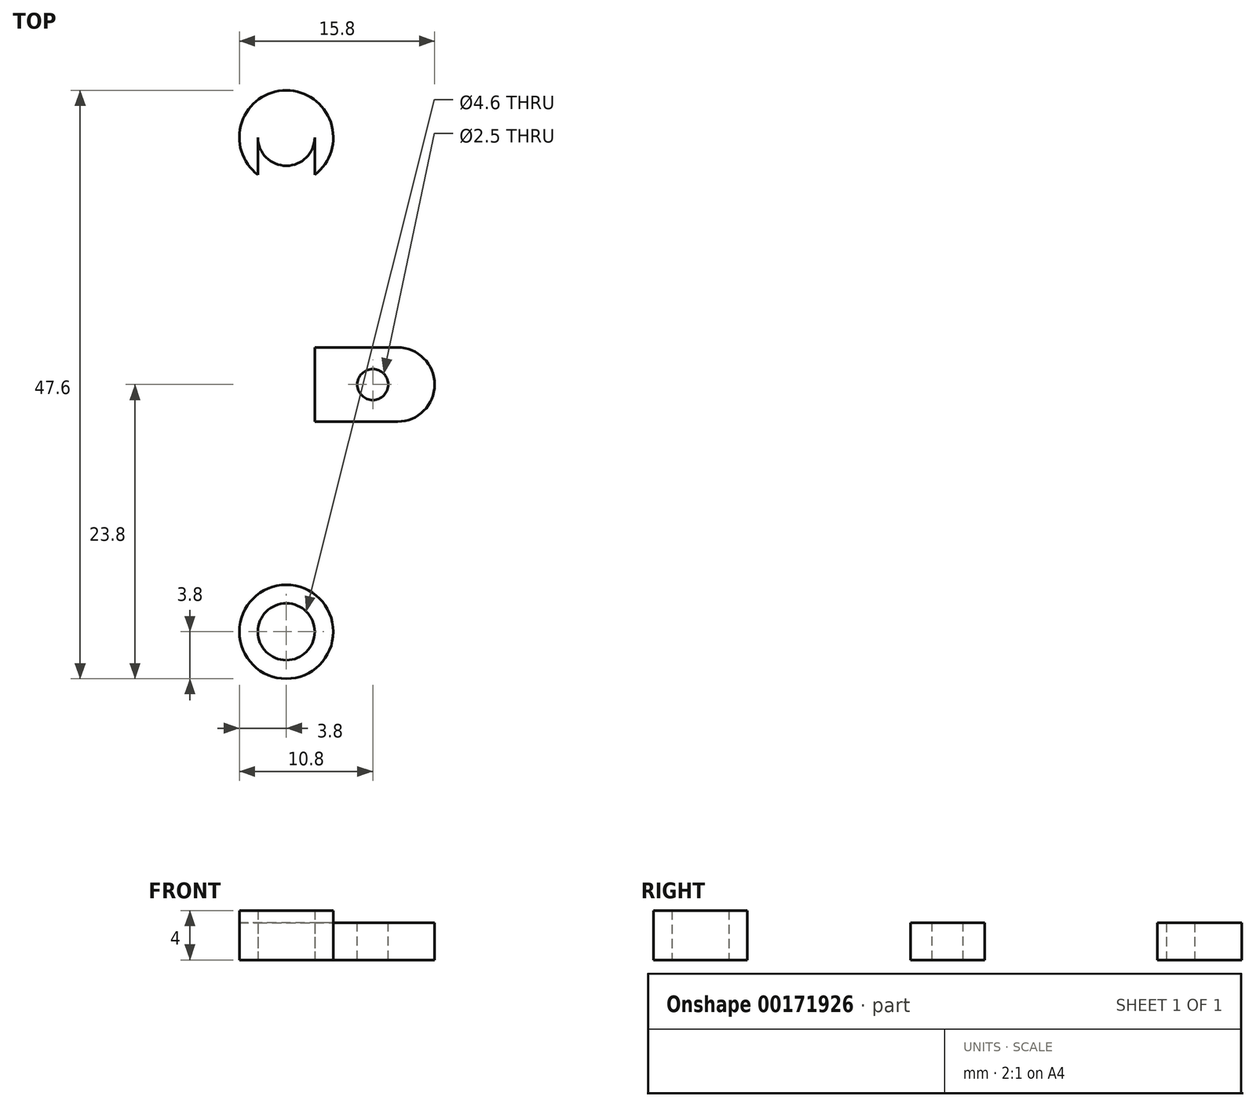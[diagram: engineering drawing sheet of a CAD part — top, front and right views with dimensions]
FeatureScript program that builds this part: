
annotation { "Feature Type Name" : "Feature", "Feature Type Description" : "" }
export const myFeature = defineFeature(function(context is Context, id is Id, definition is map)
    precondition{}
    {
        {
            var Q0;
            Q0=qCreatedBy(makeId("Top.planeOp"),FACE);
            var sketch = newSketch(context, id + "F0", { "sketchPlane" : qUnion([Q0])});
            skLineSegment(sketch, "E0.bottom", {"start": v(0, 0) * mm, "end": v(-17, 0) * mm, "construction": true});
            skLineSegment(sketch, "E0.top", {"start": v(0, 50) * mm, "end": v(-17, 50) * mm, "construction": true});
            skLineSegment(sketch, "E0.left", {"start": v(0, 0) * mm, "end": v(0, 50) * mm, "construction": true});
            skPoint(sketch, "E0.middle", {"position": v(-8.5, 25) * mm});
            skCircle(sketch, "E1", {"center": v(-12, 5) * mm, "radius": 2.3 * mm});
            skLineSegment(sketch, "E2", {"start": v(-18.53, 25) * mm, "end": v(0.77, 25) * mm, "construction": true});
            skCircle(sketch, "E3.MirrorC", {"center": v(-12, 45) * mm, "radius": 2.3 * mm});
            skLineSegment(sketch, "E4", {"start": v(-12, 50) * mm, "end": v(-8, 50) * mm});
            skLineSegment(sketch, "E5.right", {"start": v(0, 28) * mm, "end": v(0, 22) * mm});
            skCircle(sketch, "E6.0", {"center": v(-12, 45) * mm, "radius": 3.8 * mm});
            skCircle(sketch, "E7.0", {"center": v(-12, 5) * mm, "radius": 3.8 * mm});
            skLineSegment(sketch, "E8", {"start": v(-20.5, 45) * mm, "end": v(2.58, 45) * mm, "construction": true});
            skLineSegment(sketch, "E9", {"start": v(-20.08, 5) * mm, "end": v(6.27, 5) * mm, "construction": true});
            skLineSegment(sketch, "E10", {"start": v(-14.3, 45) * mm, "end": v(-14.3, 5) * mm});
            skLineSegment(sketch, "E11", {"start": v(-9.7, 5) * mm, "end": v(-9.7, 45) * mm});
            skLineSegment(sketch, "E12", {"start": v(0, 22) * mm, "end": v(-9.7, 22) * mm});
            skLineSegment(sketch, "E13", {"start": v(0, 28) * mm, "end": v(-9.7, 28) * mm});
            skSolve(sketch);
        }
        {
            var Q0;
            Q0=makeQuery(id+"F0.imprint","IMPRINT",FACE,{"disambiguationData":[TD([[makeQuery(id+"F0.imprint","IMPRINT",EDGE,{"derivedFrom":sQuery(id+"F0.wireOp",EDGE,"E5.bottom")}),-1.0]])]});
            var Q1;
            Q1=makeQuery(id+"F0.imprint","IMPRINT",FACE,{"disambiguationData":[TD([[makeQuery(id+"F0.imprint","IMPRINT",EDGE,{"derivedFrom":sQuery(id+"F0.wireOp",EDGE,"E1")}),-1.0]])]});
            var Q2;
            Q2=makeQuery(id+"F0.imprint","IMPRINT",FACE,{"disambiguationData":[TD([[makeQuery(id+"F0.imprint","IMPRINT",EDGE,{"derivedFrom":sQuery(id+"F0.wireOp",EDGE,"E3.MirrorC")}),1.0]])]});
            var Q3;
            {var subQ7=sQuery(id+"F0.wireOp",EDGE,"E5.left");Q3=makeQuery(id+"F0.imprint","IMPRINT",FACE,{"disambiguationData":[TD([[makeQuery(id+"F0.imprint","IMPRINT",EDGE,{"derivedFrom":subQ7}),-1.0]])]});}
            var Q4;
            {var subQ3=sQuery(id+"F0.wireOp",EDGE,"E6.0");var subQ5=makeQuery(id+"F0.imprint","IMPRINT",VERTEX,{"derivedFrom":subQ3});Q4=makeQuery(id+"F0.imprint","IMPRINT",FACE,{"disambiguationData":[TD([[makeQuery(id+"F0.imprint","IMPRINT",EDGE,{"disambiguationData":[TD([[subQ5,1.0]])],"derivedFrom":subQ3}),-1.0]])]});}
            var Q5;
            {var subQ4=sQuery(id+"F0.wireOp",EDGE,"E10");var subQ5=sQuery(id+"F0.wireOp",EDGE,"E6.0");var subQ6=makeQuery(id+"F0.imprint","INTERSECT",VERTEX,{"derivedFrom":[subQ5,subQ4]});Q5=makeQuery(id+"F0.imprint","IMPRINT",FACE,{"disambiguationData":[TD([[makeQuery(id+"F0.imprint","IMPRINT",EDGE,{"disambiguationData":[TD([[subQ6,1.0]])],"derivedFrom":subQ5}),1.0]])]});}
            var Q6;
            Q6=makeQuery(id+"F0.imprint","IMPRINT",FACE,{"disambiguationData":[TD([[makeQuery(id+"F0.imprint","IMPRINT",EDGE,{"derivedFrom":sQuery(id+"F0.wireOp",EDGE,"E5.right")}),-1.0]])]});
            var Q7;
            {var subQ6=sQuery(id+"F0.wireOp",EDGE,"E10");var subQ8=sQuery(id+"F0.wireOp",EDGE,"E3.MirrorC");var subQ10=makeQuery(id+"F0.imprint","INTERSECT",VERTEX,{"derivedFrom":[subQ8,subQ6]});Q7=makeQuery(id+"F0.imprint","IMPRINT",FACE,{"disambiguationData":[TD([[makeQuery(id+"F0.imprint","IMPRINT",EDGE,{"disambiguationData":[TD([[subQ10,-1.0]])],"derivedFrom":subQ8}),1.0]])]});}
            extrude(context, id + "F1", {"entities" : qUnion([Q0, Q1, Q2, Q3, Q4, Q5, Q6, Q7]), "depth" : 3 * mm});
        }
        {
            var Q0;
            Q0=makeQuery(id+"F1.opExtrude","CAP_FACE",FACE,{"disambiguationData":[OSD([sQuery(id+"F0.wireOp",EDGE,"E0.bottom"),sQuery(id+"F0.wireOp",EDGE,"E0.top"),sQuery(id+"F0.wireOp",EDGE,"E0.left"),sQuery(id+"F0.wireOp",EDGE,"E0.right"),sQuery(id+"F0.wireOp",EDGE,"E1"),sQuery(id+"F0.wireOp",EDGE,"E3.MirrorC")])],"isStart":false});
            var sketch = newSketch(context, id + "F2", { "sketchPlane" : qUnion([Q0])});
            skCircle(sketch, "E14", {"center": v(-5, 25) * mm, "radius": 1.25 * mm});
            skPoint(sketch, "E14.centerSnap0", {"position": v(-8.5, 0) * mm});
            skPoint(sketch, "E14.centerSnap1", {"position": v(0, 25) * mm});
            skSolve(sketch);
        }
        {
            var Q0;
            Q0 = qSketchRegion(id + "F2", true);
            extrude(context, id + "F3", {"entities" : qUnion([Q0]), "operationType" : NewBodyOperationType.REMOVE, "oppositeDirection" : true, "depth" : 25 * mm});
        }
        {
            var Q0;
            Q0=makeQuery(id+"F1.opExtrude","SWEPT_EDGE",EDGE,{"disambiguationData":[OSD([sQuery(id+"F0.wireOp",EDGE,"E0.left"),sQuery(id+"F0.wireOp",EDGE,"E5.top"),sQuery(id+"F0.wireOp",EDGE,"E5.right")])]});
            var Q1;
            Q1=makeQuery(id+"F1.opExtrude","SWEPT_EDGE",EDGE,{"disambiguationData":[OSD([sQuery(id+"F0.wireOp",EDGE,"E0.left"),sQuery(id+"F0.wireOp",EDGE,"E5.bottom"),sQuery(id+"F0.wireOp",EDGE,"E5.right")])]});
            fillet(context, id + "F4", {"entities" : qUnion([Q0, Q1]), "radius" : 3 * mm, "tangentPropagation" : true, "allowEdgeOverflow" : false});
        }
        {
            var Q0;
            Q0=makeQuery(id+"F1.opExtrude","CAP_FACE",FACE,{"disambiguationData":[OSD([sQuery(id+"F0.wireOp",EDGE,"E0.right"),sQuery(id+"F0.wireOp",EDGE,"E1"),sQuery(id+"F0.wireOp",EDGE,"E3.MirrorC"),sQuery(id+"F0.wireOp",EDGE,"vZfWTVAo-J0C0-PU9k-aKDK-tMiBGMtOPc1Y"),sQuery(id+"F0.wireOp",EDGE,"391sNAdQ-N0UB-zECo-Sjbo-OEPc6ZCNohZ8"),sQuery(id+"F0.wireOp",EDGE,"D4kCmrhT-G8BD-vLz4-rMwN-mygwzMj7bbxp"),sQuery(id+"F0.wireOp",EDGE,"E5.bottom"),sQuery(id+"F0.wireOp",EDGE,"E5.top"),sQuery(id+"F0.wireOp",EDGE,"E5.right")])],"isStart":false});
            var sketch = newSketch(context, id + "F5", { "sketchPlane" : qUnion([Q0])});
            skCircle(sketch, "E15", {"center": v(-12, 5) * mm, "radius": 3.8 * mm});
            skCircle(sketch, "E16", {"center": v(-12, 45) * mm, "radius": 3.8 * mm});
            skSolve(sketch);
        }
        {
            var Q0;
            Q0=makeQuery(id+"F5.imprint","IMPRINT",FACE,{"disambiguationData":[TD([[makeQuery(id+"F5.imprint","IMPRINT",EDGE,{"derivedFrom":makeQuery(id+"F1.opExtrude","CAP_EDGE",EDGE,{"disambiguationData":[OSD([sQuery(id+"F0.wireOp",EDGE,"E1")])],"isStart":false})}),-1.0]])]});
            var Q1;
            {var subQ0=sQuery(id+"F5.wireOp",EDGE,"E16");Q1=makeQuery(id+"F5.imprint","IMPRINT",FACE,{"disambiguationData":[TD([[makeQuery(id+"F5.imprint","IMPRINT",EDGE,{"disambiguationData":[OD(0.0)],"derivedFrom":subQ0}),-1.0]])]});}
            extrude(context, id + "F6", {"entities" : qUnion([Q0, Q1]), "operationType" : NewBodyOperationType.ADD, "depth" : 1 * mm});
        }
    });
